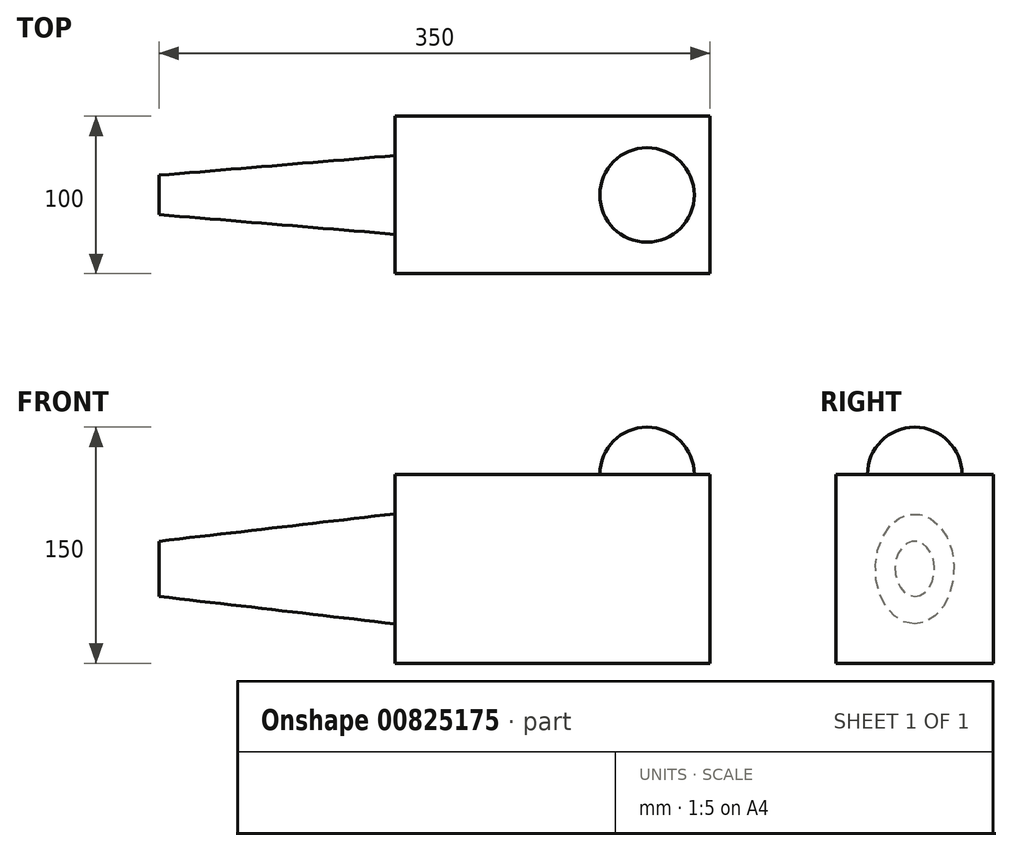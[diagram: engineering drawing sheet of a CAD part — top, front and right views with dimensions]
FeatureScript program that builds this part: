
annotation { "Feature Type Name" : "Feature", "Feature Type Description" : "" }
export const myFeature = defineFeature(function(context is Context, id is Id, definition is map)
    precondition{}
    {
        {
            var Q0;
            Q0=qCreatedBy(makeId("Top.planeOp"),FACE);
            var sketch = newSketch(context, id + "F0", { "sketchPlane" : qUnion([Q0])});
            skLineSegment(sketch, "E0.bottom", {"start": v(100, -50) * mm, "end": v(-100, -50) * mm});
            skLineSegment(sketch, "E0.top", {"start": v(100, 50) * mm, "end": v(-100, 50) * mm});
            skLineSegment(sketch, "E0.left", {"start": v(100, -50) * mm, "end": v(100, 50) * mm});
            skLineSegment(sketch, "E0.right", {"start": v(-100, -50) * mm, "end": v(-100, 50) * mm});
            skPoint(sketch, "E0.middle", {"position": v(0, 0) * mm});
            skSolve(sketch);
        }
        {
            var Q0;
            Q0=makeQuery(id+"F0.imprint","IMPRINT",FACE,{"disambiguationData":[TD([[makeQuery(id+"F0.imprint","IMPRINT",EDGE,{"derivedFrom":sQuery(id+"F0.wireOp",EDGE,"E0.bottom")}),-1.0]])]});
            extrude(context, id + "F1", {"entities" : qUnion([Q0]), "depth" : 120 * mm, "offsetDistance" : 25 * mm});
        }
        {
            var Q0;
            Q0=makeQuery(id+"F1.opExtrude","CAP_FACE",FACE,{"disambiguationData":[OSD([sQuery(id+"F0.wireOp",EDGE,"E0.bottom"),sQuery(id+"F0.wireOp",EDGE,"E0.top"),sQuery(id+"F0.wireOp",EDGE,"E0.left"),sQuery(id+"F0.wireOp",EDGE,"E0.right")])],"isStart":false});
            var sketch = newSketch(context, id + "F2", { "sketchPlane" : qUnion([Q0])});
            skArc(sketch, "E1", {"start": v(60, -30) * mm, "mid": v(90, 0) * mm, "end": v(60, 30) * mm});
            skLineSegment(sketch, "E2", {"start": v(-100, 0) * mm, "end": v(100, 0) * mm, "construction": true});
            skLineSegment(sketch, "E3", {"start": v(60, 30) * mm, "end": v(60, -30) * mm});
            skSolve(sketch);
        }
        {
            var Q0;
            Q0=makeQuery(id+"F2.imprint","IMPRINT",FACE,{"disambiguationData":[TD([[makeQuery(id+"F2.imprint","IMPRINT",EDGE,{"derivedFrom":sQuery(id+"F2.wireOp",EDGE,"E1")}),1.0]])]});
            var Q1;
            Q1=sQuery(id+"F2.wireOp",EDGE,"E3");
            revolve(context, id + "F3", {"operationType" : NewBodyOperationType.ADD, "surfaceOperationType" : NewSurfaceOperationType.NEW, "entities" : qUnion([Q0]), "axis" : qUnion([Q1]), "revolveType" : RevolveType.ONE_DIRECTION, "angle" : 180 * degree});
        }
        {
            var Q0;
            Q0=makeQuery(id+"F1.opExtrude","SWEPT_FACE",FACE,{"disambiguationData":[OSD([sQuery(id+"F0.wireOp",EDGE,"E0.right")])]});
            var sketch = newSketch(context, id + "F4", { "sketchPlane" : qUnion([Q0])});
            skLineSegment(sketch, "E4", {"start": v(-50, 60) * mm, "end": v(50, 60) * mm, "construction": true});
            skLineSegment(sketch, "E5", {"start": v(0, 120) * mm, "end": v(0, 0) * mm, "construction": true});
            skEllipse(sketch, "E6", {"center": v(0, 60) * mm, "majorRadius": 35 * mm, "minorRadius": 25 * mm, "majorAxis": v(0, -1)});
            skSolve(sketch);
        }
        {
            var Q0;
            Q0=qCreatedBy(makeId("Right.planeOp"),FACE);
            cPlane(context, id + "F5", {"entities" : qUnion([Q0]), "cplaneType" : CPlaneType.OFFSET, "offset" : 250 * mm, "oppositeDirection" : true, "width" : 150 * mm, "height" : 150 * mm});
        }
        {
            var Q0;
            Q0=qCreatedBy(id+"F5.planeOp",FACE);
            var sketch = newSketch(context, id + "F6", { "sketchPlane" : qUnion([Q0])});
            skEllipse(sketch, "E7", {"center": v(0, 60) * mm, "majorRadius": 17.5 * mm, "minorRadius": 12.5 * mm, "majorAxis": v(0, -1)});
            skSolve(sketch);
        }
        {
            var Q1;
            Q1=makeQuery(id+"F4.imprint","IMPRINT",FACE,{"disambiguationData":[TD([[makeQuery(id+"F4.imprint","IMPRINT",EDGE,{"derivedFrom":sQuery(id+"F4.wireOp",EDGE,"E6")}),1.0]])]});
            var Q2;
            Q2=makeQuery(id+"F6.imprint","IMPRINT",FACE,{"disambiguationData":[TD([[makeQuery(id+"F6.imprint","IMPRINT",EDGE,{"derivedFrom":sQuery(id+"F6.wireOp",EDGE,"E7")}),1.0]])]});
            loft(context, id + "F7", {"operationType" : NewBodyOperationType.ADD, "sheetProfilesArray" : [{ "sheetProfileEntities" : qUnion([Q1]) }, { "sheetProfileEntities" : qUnion([Q2]) }]});
        }
    });
